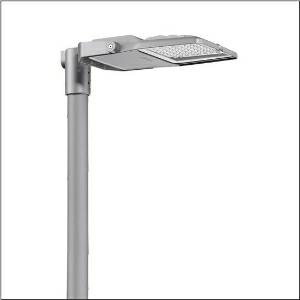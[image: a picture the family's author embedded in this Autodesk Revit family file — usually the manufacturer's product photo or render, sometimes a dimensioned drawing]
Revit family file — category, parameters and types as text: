
# Revit family: floodlight_fl_21_iq_mini___pl52_5xa7771b2d3a_cd8f
name_source: partatom
category: Lighting Fixtures
units: mm (PartAtom-declared; Revit-internal decimal feet)

## family parameters
Cut with Voids When Loaded = No
Host = Face
Light Source = No
Part Type = Normal
Room Calculation Point = No
Round Connector Dimension = Use Diameter
Shared = No

## types (1)
- --- (1 x LED, 6240 lm, 45.5 W, 3000K)
    Apparent Load = 46 VA
    CIE Flux Codes = 26 60 98 100 100
    Color Rendering = 70
    Color Temperature = 3000K
    Default Elevation = 1800 mm
    Description = Floodlight FL 21 iQ mini, floodlight, primary light control with lens, of PMMA, primary optical cover: protective disc, of toughened safety glass, transparent, light distribution: PL52, light emission: direct distribution, installation type: surface-mounted, LED, High Power LED, rated luminous flux: 6.240lm, luminous efficacy: 137lm/W, light colour: 730, colour temperature: 3000K, control gear: iQ Comfort/DALI, control: Auto-Match, Temp-Guard, Lumen-Switch, Night-Set, Smart-Wire, Light-Fading, Desk-Remote (wireless, voltage-free reading and setting of iQ features in the workshop via application-optimized NFC function/RFID function), optimised constant luminous flux control (CLO 2.0), with terminal, 6-pole, mains connection: 220..240V, AC, 50/60Hz, start of lifetime: 46W, end of service life: 48W, reduction: 22W, luminaire housing, of diecast aluminium, powder-coated, Siteco® metallic grey (DB 702S), corrosivity category C5 mid according to DIN EN ISO 12944, suitable for swimming pools, chlorine-resistant, sealing non-destructively replaceable, please order mast flange separately, mast bracket, of steel, galvanised, powder-coated, Siteco® metallic grey (DB 702S), protection rating (complete): IP66, insulation class (complete): insulation class II (safety insulation), certification: CE, ENEC, VDE, protection symbol: D, impact resistance: IK08, permissible operating ambient temperature: -40..+40°C, permissible operating ambient temperature for outdoor applications: -40..+50°C, standard: DIN EN 12944, LABS conformity tested according to VDMA 24364:2018-05, packaging unit: 1 piece

Light Distribution: PL52
    Height = 70 mm
    Lamp = 1 x LED
    Lamp Light Flux = 6240 lm
    Lamp Power = 45.5 W
    Lamp count = 1
    Length = 485 mm
    Luminous efficacy = 137 lm/W
    Manufacturer = Siteco
    ModVariant = No
    Model = 5XA7771B2D3A
    Number of Poles = 1
    OnlyDefault = Yes
    Power Factor = 1
    Product Name = Floodlight FL 21 iQ mini | PL52
    Product group = floodlight | pylon annexe
    ProductGroupID = 6201
    Protection Class = Protection class II
    Protection Degree = IP 66
    RLX_Detail_Level = 1
    RLX_Emergency_Light_Flux = 0 lm
    RLX_Emergency_Type = 0
    RLX_Emergency_Type_DB = No
    RlxData = <blob elided: 101401 chars, md5=3706c15a>
    Socket = socket
    Standby Power = 0 W
    System Light Flux = 6240 lm
    System Power = 46 W
    Type Comments = factory setting: luminous flux: 100 % | dim-lin: 254 | 463 mA
    Type Image = l_1007125.jpg
    URL = http://relux.com
    VarID = @adj_186553
    Voltage = 0 V
    Weight = 0.00 kg
    Width = 337 mm

## geometry (parser evidence)
native form markers: Blend x4, Sweep x14
no freeform markers — native parametric forms only
